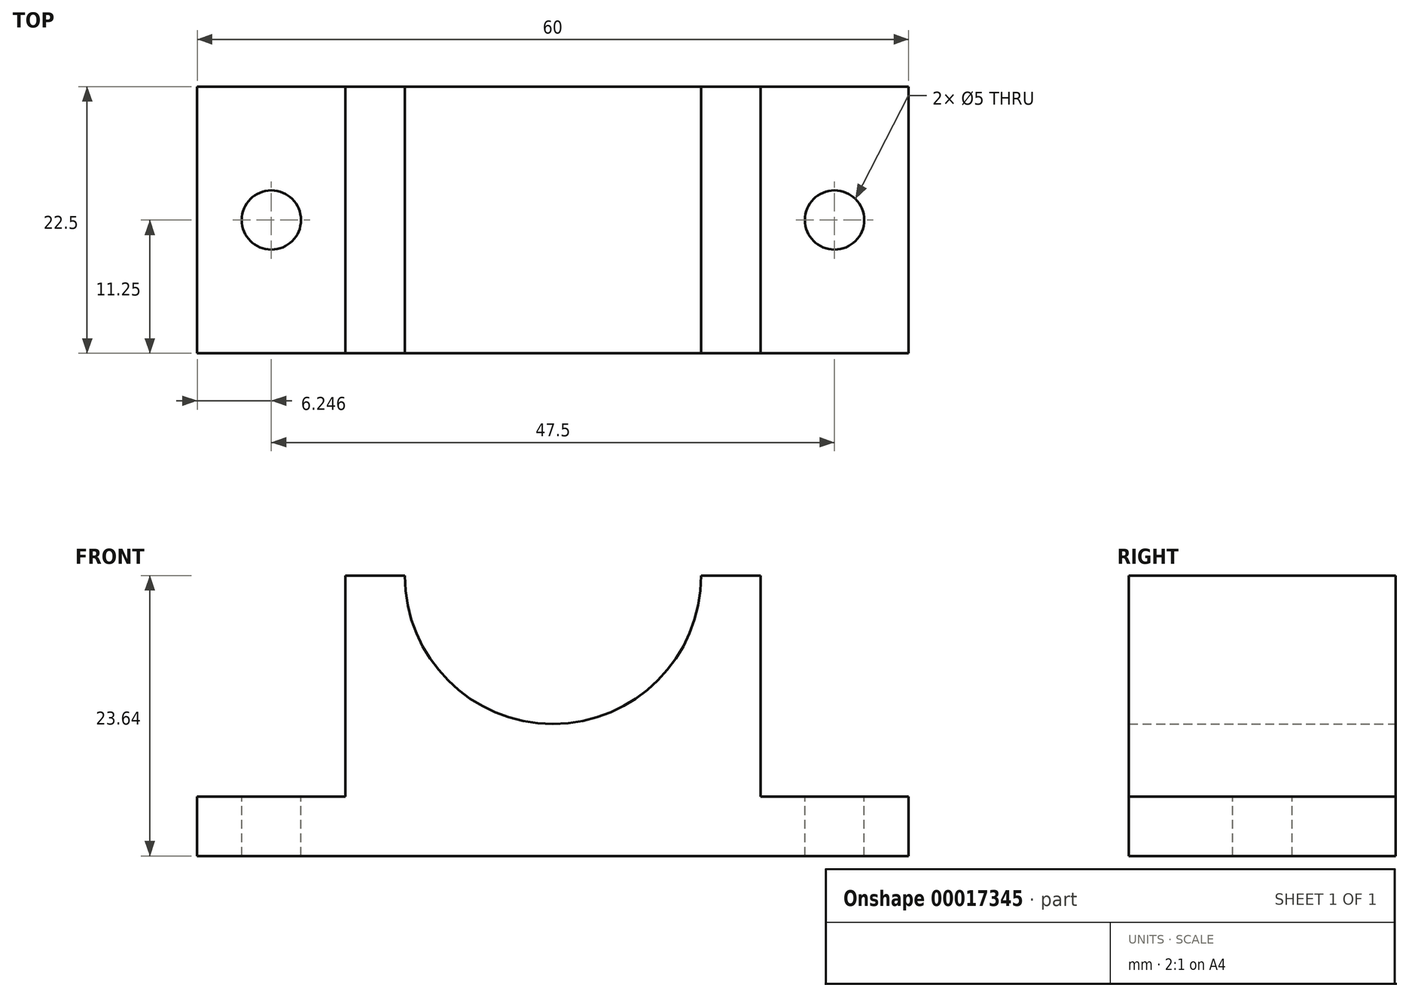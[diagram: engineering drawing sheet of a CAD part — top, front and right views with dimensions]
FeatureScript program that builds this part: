
annotation { "Feature Type Name" : "Feature", "Feature Type Description" : "" }
export const myFeature = defineFeature(function(context is Context, id is Id, definition is map)
    precondition{}
    {
        {
            var Q0;
            Q0=qCreatedBy(makeId("Front.planeOp"),FACE);
            var sketch = newSketch(context, id + "F0", { "sketchPlane" : qUnion([Q0])});
            skLineSegment(sketch, "E0", {"start": v(-25.03, -16.48) * mm, "end": v(-25.03, -21.48) * mm});
            skLineSegment(sketch, "E1", {"start": v(-25.03, -21.48) * mm, "end": v(34.97, -21.48) * mm});
            skLineSegment(sketch, "E2", {"start": v(34.97, -21.48) * mm, "end": v(34.97, -16.48) * mm});
            skLineSegment(sketch, "E3", {"start": v(34.97, -16.48) * mm, "end": v(22.47, -16.48) * mm});
            skLineSegment(sketch, "E4", {"start": v(22.47, -16.48) * mm, "end": v(22.47, 2.16) * mm});
            skLineSegment(sketch, "E5", {"start": v(22.47, 2.16) * mm, "end": v(-12.53, 2.16) * mm});
            skLineSegment(sketch, "E6", {"start": v(-12.53, 2.16) * mm, "end": v(-12.53, -16.48) * mm});
            skLineSegment(sketch, "E7", {"start": v(-12.53, -16.48) * mm, "end": v(-25.03, -16.48) * mm});
            skArc(sketch, "E8", {"start": v(-7.53, 2.16) * mm, "mid": v(4.97, -10.34) * mm, "end": v(17.47, 2.16) * mm});
            skSolve(sketch);
        }
        {
            var Q0;
            Q0=makeQuery(id+"F0.imprint","IMPRINT",FACE,{"disambiguationData":[TD([[makeQuery(id+"F0.imprint","IMPRINT",EDGE,{"derivedFrom":sQuery(id+"F0.wireOp",EDGE,"E0")}),1.0]])]});
            extrude(context, id + "F1", {"entities" : qUnion([Q0]), "depth" : 22.5 * mm});
        }
        {
            var Q0;
            Q0=makeQuery(id+"F1.opExtrude","SWEPT_FACE",FACE,{"disambiguationData":[OSD([sQuery(id+"F0.wireOp",EDGE,"E3")])]});
            var sketch = newSketch(context, id + "F2", { "sketchPlane" : qUnion([Q0])});
            skCircle(sketch, "E9", {"center": v(28.72, -11.25) * mm, "radius": 2.5 * mm});
            skCircle(sketch, "E10", {"center": v(-18.78, -11.25) * mm, "radius": 2.5 * mm});
            skSolve(sketch);
        }
        {
            var Q0;
            Q0=sQuery(id+"F2.wireOp",VERTEX,"E9.center");
            var Q1;
            Q1=makeQuery(id+"F1.opExtrude","SWEPT_BODY",BODY,{"disambiguationData":[OSD([sQuery(id+"F0.wireOp",EDGE,"E0"),sQuery(id+"F0.wireOp",EDGE,"E1"),sQuery(id+"F0.wireOp",EDGE,"E2"),sQuery(id+"F0.wireOp",EDGE,"E3"),sQuery(id+"F0.wireOp",EDGE,"E4"),sQuery(id+"F0.wireOp",EDGE,"E5"),sQuery(id+"F0.wireOp",EDGE,"E6"),sQuery(id+"F0.wireOp",EDGE,"E7"),sQuery(id+"F0.wireOp",EDGE,"E8")])]});
            hole(context, id + "F3", {"style" : HoleStyle.SIMPLE, "holeDiameter" : 5 * mm, "endStyle" : HoleEndStyle.THROUGH, "locations" : qUnion([Q0]), "scope" : qUnion([Q1])});
        }
        {
            var Q0;
            Q0 = qSketchRegion(id + "F2", true);
            extrude(context, id + "F4", {"entities" : qUnion([Q0]), "operationType" : NewBodyOperationType.REMOVE, "oppositeDirection" : true, "depth" : 25 * mm});
        }
    });
